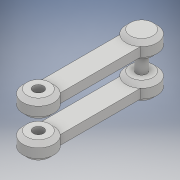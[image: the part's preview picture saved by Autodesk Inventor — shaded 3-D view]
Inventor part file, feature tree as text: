
AUTODESK INVENTOR PART (.ipt)
format: ipt  version: 2018 (Build 220112000, 112)  size: 155,136 bytes
history: native  units: mm
features: extrude x4, other x1, sketch x1, chamfer x1
ambient origin geometry x8: Origin, YZ Plane, XZ Plane, XY Plane, X Axis, Y Axis, Z Axis, Center Point
bodies: Body1 (feature_tree)
feature tree (7):
  other  "Твердое тело1"
  sketch  "Эскиз1"
  extrude  "Выдавливание1"  Depth=15.0mm
  extrude  "Выдавливание2"  Depth=15.0mm
  extrude  "Выдавливание3"  Depth=5.0mm
  extrude  "Выдавливание4"  Depth=5.0mm
  chamfer  "Фаска1"  Distance=22.0mm
